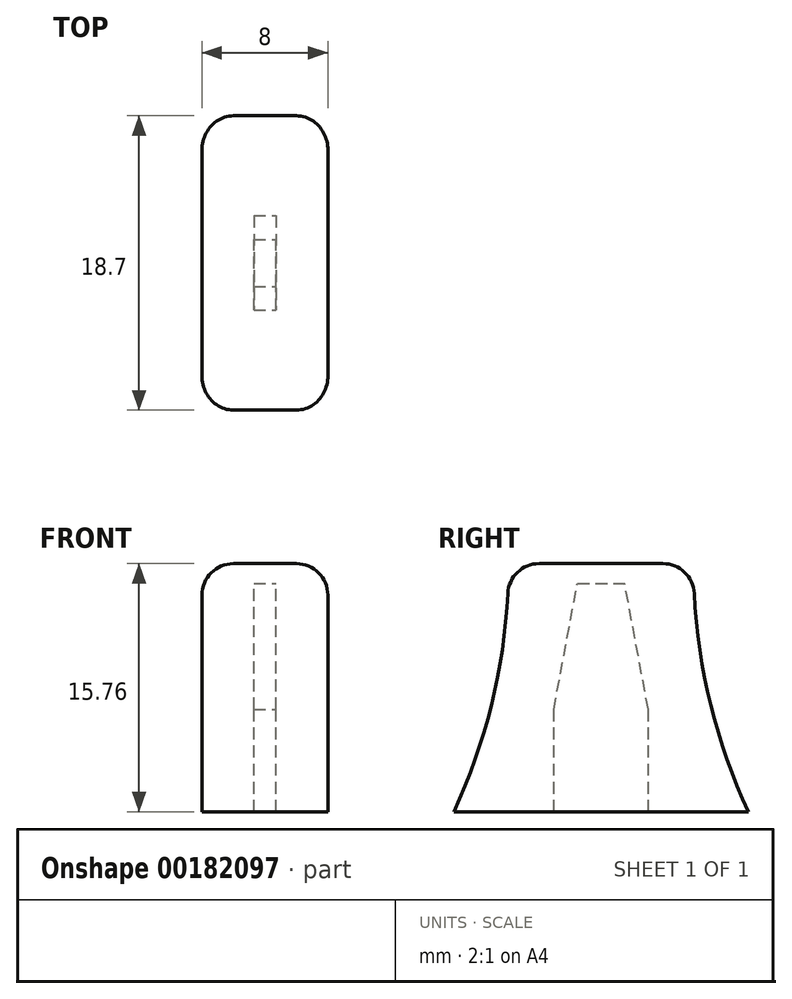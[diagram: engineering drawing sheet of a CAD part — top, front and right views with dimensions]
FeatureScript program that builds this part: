
annotation { "Feature Type Name" : "Feature", "Feature Type Description" : "" }
export const myFeature = defineFeature(function(context is Context, id is Id, definition is map)
    precondition{}
    {
        {
            var Q0;
            Q0=qCreatedBy(makeId("Right.planeOp"),FACE);
            var sketch = newSketch(context, id + "F0", { "sketchPlane" : qUnion([Q0])});
            skLineSegment(sketch, "E0.bottom", {"start": v(0, 0) * mm, "end": v(-9.35, 0) * mm});
            skLineSegment(sketch, "E0.top", {"start": v(0, 15.76) * mm, "end": v(-9.35, 15.76) * mm});
            skLineSegment(sketch, "E0.left", {"start": v(0, 0) * mm, "end": v(0, 15.76) * mm});
            skLineSegment(sketch, "E0.right", {"start": v(-9.35, 0) * mm, "end": v(-9.35, 15.76) * mm});
            skSolve(sketch);
        }
        {
            var Q0;
            Q0=makeQuery(id+"F0.imprint","IMPRINT",FACE,{"disambiguationData":[TD([[makeQuery(id+"F0.imprint","IMPRINT",EDGE,{"derivedFrom":sQuery(id+"F0.wireOp",EDGE,"E0.bottom")}),-1.0]])]});
            extrude(context, id + "F1", {"entities" : qUnion([Q0]), "depth" : 8 * mm, "symmetric" : true});
        }
        {
            var Q0;
            Q0=qCreatedBy(makeId("Right.planeOp"),FACE);
            var sketch = newSketch(context, id + "F2", { "sketchPlane" : qUnion([Q0])});
            skCircle(sketch, "E1", {"center": v(-43.37, 15.76) * mm, "radius": 37.5 * mm});
            skSolve(sketch);
        }
        {
            var Q0;
            Q0 = qSketchRegion(id + "F2", true);
            extrude(context, id + "F3", {"entities" : qUnion([Q0]), "operationType" : NewBodyOperationType.REMOVE, "endBound" : BoundingType.THROUGH_ALL, "oppositeDirection" : true, "depth" : 25 * mm, "hasSecondDirection" : true, "secondDirectionBound" : BoundingType.THROUGH_ALL, "secondDirectionOppositeDirection" : false, "secondDirectionDepth" : 25 * mm});
        }
        {
            var Q0;
            Q0=makeQuery(id+"F3.boolean.opBoolean","INTERSECT",EDGE,{"derivedFrom":[makeQuery(id+"F1.opExtrude","SWEPT_FACE",FACE,{"disambiguationData":[OSD([sQuery(id+"F0.wireOp",EDGE,"E0.top")])]}),makeQuery(id+"F3.opExtrude","SWEPT_FACE",FACE,{"disambiguationData":[OSD([sQuery(id+"F2.wireOp",EDGE,"E1")])]})]});
            var Q1;
            Q1=makeQuery(id+"F3.boolean.opBoolean","INTERSECT",EDGE,{"derivedFrom":[makeQuery(id+"F1.opExtrude","CAP_FACE",FACE,{"disambiguationData":[OSD([sQuery(id+"F0.wireOp",EDGE,"E0.bottom"),sQuery(id+"F0.wireOp",EDGE,"E0.top"),sQuery(id+"F0.wireOp",EDGE,"E0.left"),sQuery(id+"F0.wireOp",EDGE,"E0.right")])],"isStart":false}),makeQuery(id+"F3.opExtrude","SWEPT_FACE",FACE,{"disambiguationData":[OSD([sQuery(id+"F2.wireOp",EDGE,"E1")])]})]});
            var Q2;
            Q2=makeQuery(id+"F3.boolean.opBoolean","INTERSECT",EDGE,{"derivedFrom":[makeQuery(id+"F1.opExtrude","CAP_FACE",FACE,{"disambiguationData":[OSD([sQuery(id+"F0.wireOp",EDGE,"E0.bottom"),sQuery(id+"F0.wireOp",EDGE,"E0.top"),sQuery(id+"F0.wireOp",EDGE,"E0.left"),sQuery(id+"F0.wireOp",EDGE,"E0.right")])],"isStart":true}),makeQuery(id+"F3.opExtrude","SWEPT_FACE",FACE,{"disambiguationData":[OSD([sQuery(id+"F2.wireOp",EDGE,"E1")])]})]});
            var Q3;
            Q3=makeQuery(id+"F1.opExtrude","CAP_EDGE",EDGE,{"disambiguationData":[OSD([sQuery(id+"F0.wireOp",EDGE,"E0.top")])],"isStart":false});
            var Q4;
            Q4=makeQuery(id+"F1.opExtrude","CAP_EDGE",EDGE,{"disambiguationData":[OSD([sQuery(id+"F0.wireOp",EDGE,"E0.top")])],"isStart":true});
            var Q5;
            Q5=makeQuery(id+"F1.opExtrude","SWEPT_EDGE",EDGE,{"disambiguationData":[OSD([sQuery(id+"F0.wireOp",EDGE,"E0.bottom"),sQuery(id+"F0.wireOp",EDGE,"E0.right")])]});
            fillet(context, id + "F4", {"entities" : qUnion([Q0, Q1, Q2, Q3, Q4, Q5]), "radius" : 2 * mm, "tangentPropagation" : true, "allowEdgeOverflow" : false});
        }
        {
            var Q0;
            Q0=qCreatedBy(makeId("Right.planeOp"),FACE);
            var sketch = newSketch(context, id + "F5", { "sketchPlane" : qUnion([Q0])});
            skLineSegment(sketch, "E2", {"start": v(0, 0) * mm, "end": v(-3, 0) * mm});
            skLineSegment(sketch, "E3", {"start": v(-3, 0) * mm, "end": v(-3, 6.5) * mm});
            skLineSegment(sketch, "E4", {"start": v(-1.5, 14.5) * mm, "end": v(0, 14.5) * mm});
            skLineSegment(sketch, "E5", {"start": v(0, 14.5) * mm, "end": v(0, 0) * mm});
            skLineSegment(sketch, "E6", {"start": v(-3, 6.5) * mm, "end": v(-1.5, 14.5) * mm});
            skSolve(sketch);
        }
        {
            var Q0;
            Q0 = qSketchRegion(id + "F5", true);
            extrude(context, id + "F6", {"entities" : qUnion([Q0]), "operationType" : NewBodyOperationType.REMOVE, "oppositeDirection" : true, "depth" : 1.4 * mm, "symmetric" : true});
        }
        {
            var Q0;
            Q0=makeQuery(id+"F1.opExtrude","SWEPT_BODY",BODY,{"disambiguationData":[OSD([sQuery(id+"F0.wireOp",EDGE,"E0.bottom"),sQuery(id+"F0.wireOp",EDGE,"E0.top"),sQuery(id+"F0.wireOp",EDGE,"E0.left"),sQuery(id+"F0.wireOp",EDGE,"E0.right")])]});
            var Q1;
            Q1=qCreatedBy(makeId("Front.planeOp"),FACE);
            mirror(context, id + "F7", {"operationType" : NewBodyOperationType.ADD, "entities" : qUnion([Q0]), "mirrorPlane" : qUnion([Q1])});
        }
    });
